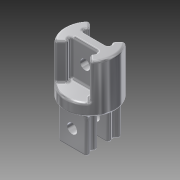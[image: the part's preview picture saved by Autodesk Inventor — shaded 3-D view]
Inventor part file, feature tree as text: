
AUTODESK INVENTOR PART (.ipt)
format: ipt  version: 2013 (Build 170138000, 138)  size: 972,800 bytes
history: native  units: mm
features: extrude x4, other x2, folder x1, plane x1, fillet x1, sketch x1
ambient origin geometry x8: Origin, YZ Plane, XZ Plane, XY Plane, X Axis, Y Axis, Z Axis, Center Point
bodies: Solid1 (feature_tree)
feature tree (10):
  folder  "Master Lengths"
  other  "Profile"
  extrude  "Plug Side"  Depth=2.0mm
  extrude  "Fuse Section"  Depth=12.7mm
  plane  "Work Plane2"
  extrude  "Clamp Side Extrude"  Depth=4.0mm
  fillet  "Fillet1"  [1 undecoded]
  extrude  "Extrusion6"  TaperAngle=45.0deg  [1 undecoded]
  other  "Clamp Side"
  sketch  "Sketch6"  dims[d0=4.0mm d2=2.0mm d3=12.7mm d4=4.0mm d5=45.0deg d6=45.0deg d7=15.0mm d8=0.0mm d9=5.0mm d10=0.0mm d11=0.0mm d12=12.0mm d13=12.0mm d14=15.0mm d16=15.0mm d18=20.0mm d19=25.0mm d21=5.0mm d23=-5.0mm d24=15.0mm d25=0.0mm d26=1.0mm d27=1.0mm d54=4.0mm d56=4.0mm d57=7.5mm d58=7.5mm d59=7.5mm d60=7.5mm d61=0.0mm d62=0.0mm d63=20.0mm d64=0.0mm]
note: 2 required parameter values undecoded (feature->parameter linkage not recoverable at this tier; creation-order binding heuristic only, values carry confidence <= 0.55)
